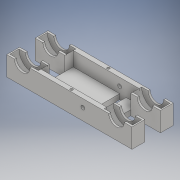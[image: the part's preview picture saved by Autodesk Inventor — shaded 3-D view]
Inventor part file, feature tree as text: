
AUTODESK INVENTOR PART (.ipt)
format: ipt  version: 2017 (Build 210142000, 142)  size: 274,432 bytes
history: native  units: mm
features: mirror x10, extrude x8, sketch x6, other x5
ambient origin geometry x8: Origin, YZ Plane, XZ Plane, XY Plane, X Axis, Y Axis, Z Axis, Center Point
bodies: Body1 (feature_tree)
feature tree (29):
  other  "Твердое тело1"
  extrude  "Выдавливание1"  Depth=8.0mm
  extrude  "Выдавливание2"  Depth=22.0mm
  extrude  "Выдавливание3"  Depth=1.0mm
  other  "РабПлоскость5"
  mirror  "Зеркальное отражение7"
  mirror  "Зеркальное отражение8"
  other  "РабПлоскость10"
  mirror  "Зеркальное отражение9"
  mirror  "Зеркальное отражение10"
  other  "РабПлоскость11"
  mirror  "Зеркальное отражение11"
  mirror  "Зеркальное отражение12"
  extrude  "Выдавливание11"  Depth=15.0mm
  other  "РабПлоскость14"
  extrude  "Выдавливание12"  Depth=32.0mm TaperAngle=0.0deg
  mirror  "Зеркальное отражение15"
  extrude  "Выдавливание13"  Depth=12.0mm
  mirror  "Зеркальное отражение16"
  mirror  "Зеркальное отражение17"
  extrude  "Выдавливание15"  Depth=1.5mm TaperAngle=0.0deg
  mirror  "Зеркальное отражение18"
  extrude  "Выдавливание17"  Depth=1.5mm TaperAngle=0.0deg
  sketch  "Эскиз2"
  sketch  "Эскиз14"
  sketch  "Эскиз15"
  sketch  "Эскиз16"
  sketch  "Эскиз19"
  sketch  "Эскиз20"
